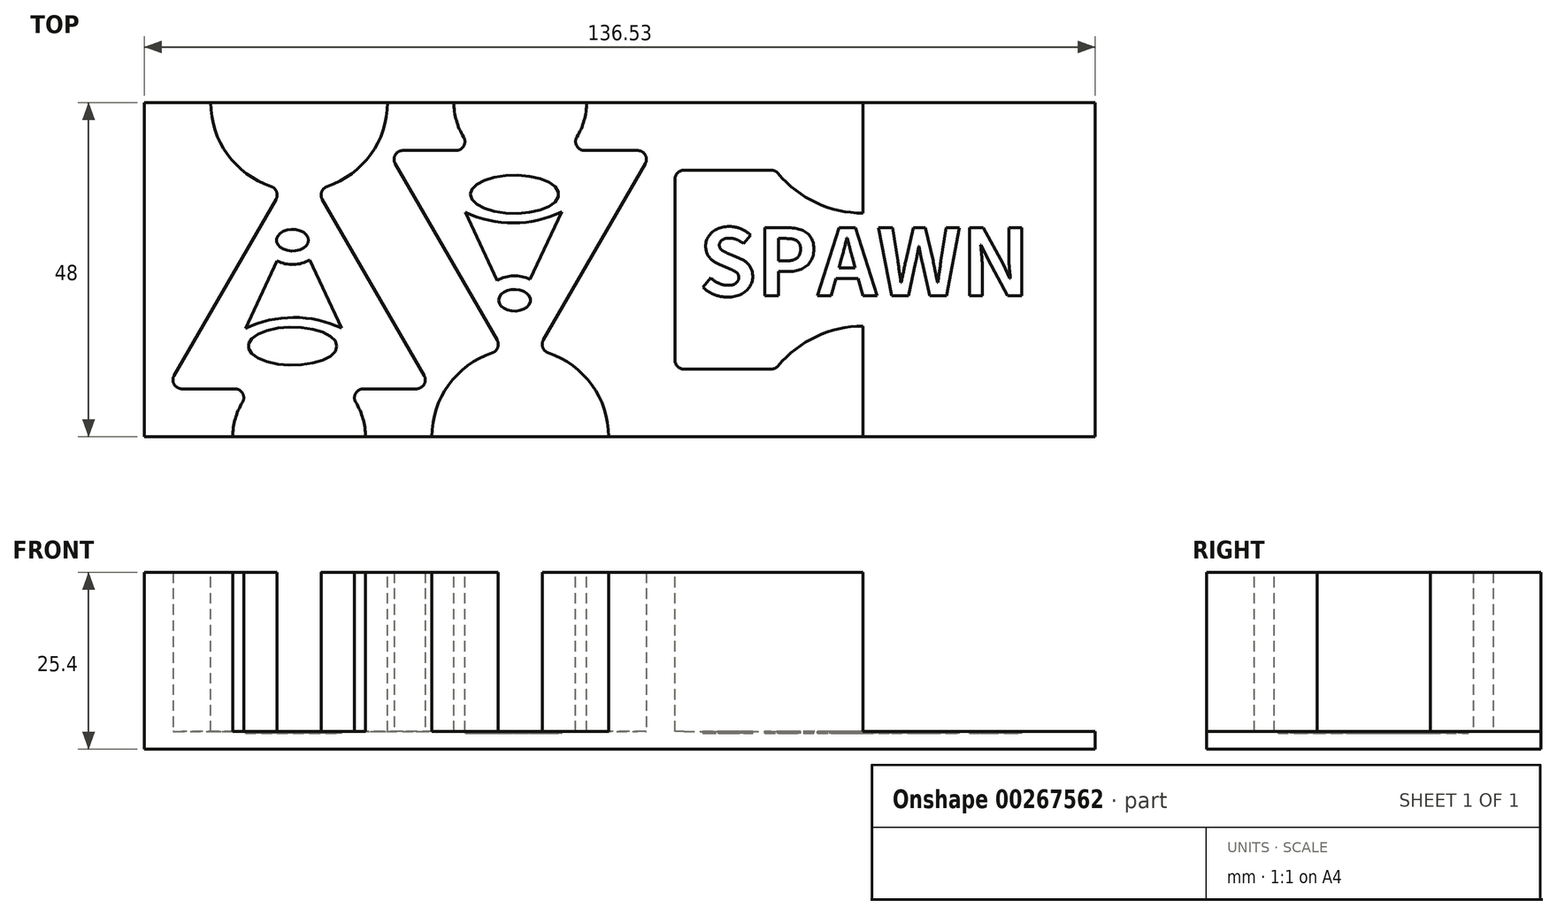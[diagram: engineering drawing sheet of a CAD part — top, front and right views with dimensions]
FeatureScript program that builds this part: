
annotation { "Feature Type Name" : "Feature", "Feature Type Description" : "" }
export const myFeature = defineFeature(function(context is Context, id is Id, definition is map)
    precondition{}
    {
        {
            var Q0;
            Q0=qCreatedBy(makeId("Top.planeOp"),FACE);
            var sketch = newSketch(context, id + "F0", { "sketchPlane" : qUnion([Q0])});
            skLineSegment(sketch, "E0.bottom", {"start": v(0, 0) * mm, "end": v(136.53, 0) * mm});
            skLineSegment(sketch, "E0.top", {"start": v(0, 48) * mm, "end": v(136.53, 48) * mm});
            skLineSegment(sketch, "E0.left", {"start": v(0, 0) * mm, "end": v(0, 48) * mm});
            skLineSegment(sketch, "E0.right", {"start": v(136.53, 0) * mm, "end": v(136.53, 48) * mm});
            skSolve(sketch);
        }
        {
            var Q0;
            Q0=makeQuery(id+"F0.imprint","IMPRINT",FACE,{"disambiguationData":[TD([[makeQuery(id+"F0.imprint","IMPRINT",EDGE,{"derivedFrom":sQuery(id+"F0.wireOp",EDGE,"E0.bottom")}),1.0]])]});
            extrude(context, id + "F1", {"entities" : qUnion([Q0]), "depth" : 25.4 * mm});
        }
        {
            var Q0;
            Q0=makeQuery(id+"F1.opExtrude","CAP_FACE",FACE,{"disambiguationData":[OSD([sQuery(id+"F0.wireOp",EDGE,"E0.bottom"),sQuery(id+"F0.wireOp",EDGE,"E0.top"),sQuery(id+"F0.wireOp",EDGE,"E0.left"),sQuery(id+"F0.wireOp",EDGE,"E0.right")])],"isStart":false});
            var sketch = newSketch(context, id + "F2", { "sketchPlane" : qUnion([Q0])});
            skCircle(sketch, "E1.cCircle", {"center": v(22.23, 17.88) * mm, "radius": 11 * mm, "construction": true});
            skLineSegment(sketch, "E1.0", {"start": v(22.23, 39.87) * mm, "end": v(41.28, 6.88) * mm});
            skLineSegment(sketch, "E1.1", {"start": v(41.28, 6.88) * mm, "end": v(3.18, 6.88) * mm});
            skLineSegment(sketch, "E1.2", {"start": v(3.17, 6.88) * mm, "end": v(22.23, 39.87) * mm});
            skPoint(sketch, "E1.0.midPoint", {"position": v(31.75, 23.38) * mm});
            skLineSegment(sketch, "E2", {"start": v(0, 24) * mm, "end": v(136.53, 24) * mm, "construction": true});
            skPoint(sketch, "E2.startSnap0", {"position": v(0, 24) * mm});
            skLineSegment(sketch, "E3", {"start": v(22.23, 48) * mm, "end": v(22.23, 0) * mm, "construction": true});
            skPoint(sketch, "E3.endSnap0", {"position": v(22.23, 6.88) * mm});
            skCircle(sketch, "E4", {"center": v(22.23, 48) * mm, "radius": 12.7 * mm});
            skCircle(sketch, "E5", {"center": v(22.22, 0) * mm, "radius": 9.53 * mm});
            skCircle(sketch, "E6.cCircle", {"center": v(53.97, 30.12) * mm, "radius": 11 * mm, "construction": true});
            skLineSegment(sketch, "E6.0", {"start": v(53.98, 8.12) * mm, "end": v(34.93, 41.12) * mm});
            skLineSegment(sketch, "E6.1", {"start": v(34.93, 41.12) * mm, "end": v(73.02, 41.12) * mm});
            skLineSegment(sketch, "E6.2", {"start": v(73.02, 41.12) * mm, "end": v(53.97, 8.13) * mm});
            skPoint(sketch, "E6.0.midPoint", {"position": v(44.45, 24.62) * mm});
            skLineSegment(sketch, "E7", {"start": v(136.53, 24) * mm, "end": v(0, 24) * mm, "construction": true});
            skPoint(sketch, "E7.startSnap0", {"position": v(122.49, -12.24) * mm});
            skLineSegment(sketch, "E8", {"start": v(53.98, 0) * mm, "end": v(53.98, 48) * mm, "construction": true});
            skPoint(sketch, "E8.endSnap0", {"position": v(53.98, 41.12) * mm});
            skCircle(sketch, "E9", {"center": v(53.98, 0) * mm, "radius": 12.7 * mm});
            skCircle(sketch, "E10", {"center": v(53.98, 48) * mm, "radius": 9.53 * mm});
            skLineSegment(sketch, "E11.bottom", {"start": v(76.2, 38.29) * mm, "end": v(130.17, 38.29) * mm});
            skLineSegment(sketch, "E11.top", {"start": v(76.2, 9.71) * mm, "end": v(130.17, 9.71) * mm});
            skLineSegment(sketch, "E11.left", {"start": v(76.2, 38.29) * mm, "end": v(76.2, 9.71) * mm});
            skLineSegment(sketch, "E11.right", {"start": v(130.18, 38.29) * mm, "end": v(130.18, 9.71) * mm});
            skCircle(sketch, "E12", {"center": v(103.19, 48) * mm, "radius": 15.88 * mm});
            skPoint(sketch, "E13.startSnap0", {"position": v(103.19, 9.71) * mm});
            skLineSegment(sketch, "E14", {"start": v(103.19, 0) * mm, "end": v(103.19, 48) * mm});
            skCircle(sketch, "E15", {"center": v(103.19, 0) * mm, "radius": 15.88 * mm});
            skSolve(sketch);
        }
        {
            var Q0;
            {var subQ1=sQuery(id+"F2.wireOp",EDGE,"E1.1");var subQ7=sQuery(id+"F2.wireOp",EDGE,"E1.0");var subQ8=makeQuery(id+"F2.imprint","INTERSECT",VERTEX,{"derivedFrom":[subQ7,subQ1]});Q0=makeQuery(id+"F2.imprint","IMPRINT",FACE,{"disambiguationData":[TD([[makeQuery(id+"F2.imprint","IMPRINT",EDGE,{"disambiguationData":[TD([[subQ8,1.0]])],"derivedFrom":subQ7}),-1.0]])]});}
            var Q1;
            {var subQ0=sQuery(id+"F2.wireOp",EDGE,"E5");var subQ1=sQuery(id+"F2.wireOp",EDGE,"E1.1");var subQ2=makeQuery(id+"F2.imprint","INTERSECT",VERTEX,{"disambiguationData":[OD(0.0)],"derivedFrom":[subQ1,subQ0]});Q1=makeQuery(id+"F2.imprint","IMPRINT",FACE,{"disambiguationData":[TD([[makeQuery(id+"F2.imprint","IMPRINT",EDGE,{"disambiguationData":[TD([[subQ2,-1.0]])],"derivedFrom":subQ1}),-1.0]])]});}
            var Q2;
            {var subQ0=sQuery(id+"F2.wireOp",EDGE,"E5");var subQ1=sQuery(id+"F2.wireOp",EDGE,"E1.1");var subQ2=makeQuery(id+"F2.imprint","INTERSECT",VERTEX,{"disambiguationData":[OD(0.0)],"derivedFrom":[subQ1,subQ0]});Q2=makeQuery(id+"F2.imprint","IMPRINT",FACE,{"disambiguationData":[TD([[makeQuery(id+"F2.imprint","IMPRINT",EDGE,{"disambiguationData":[TD([[subQ2,-1.0]])],"derivedFrom":subQ1}),1.0]])]});}
            var Q3;
            {var subQ1=sQuery(id+"F2.wireOp",EDGE,"E1.0");var subQ5=sQuery(id+"F2.wireOp",EDGE,"E1.2");var subQ8=makeQuery(id+"F2.imprint","INTERSECT",VERTEX,{"derivedFrom":[subQ1,subQ5]});Q3=makeQuery(id+"F2.imprint","IMPRINT",FACE,{"disambiguationData":[TD([[makeQuery(id+"F2.imprint","IMPRINT",EDGE,{"disambiguationData":[TD([[subQ8,-1.0]])],"derivedFrom":subQ1}),1.0]])]});}
            var Q4;
            {var subQ0=sQuery(id+"F2.wireOp",EDGE,"E1.2");var subQ1=sQuery(id+"F2.wireOp",EDGE,"E1.0");var subQ2=makeQuery(id+"F2.imprint","INTERSECT",VERTEX,{"derivedFrom":[subQ1,subQ0]});Q4=makeQuery(id+"F2.imprint","IMPRINT",FACE,{"disambiguationData":[TD([[makeQuery(id+"F2.imprint","IMPRINT",EDGE,{"disambiguationData":[TD([[subQ2,-1.0]])],"derivedFrom":subQ1}),-1.0]])]});}
            var Q5;
            {var subQ0=sQuery(id+"F2.wireOp",EDGE,"E10");var subQ1=sQuery(id+"F2.wireOp",EDGE,"E6.1");var subQ2=makeQuery(id+"F2.imprint","INTERSECT",VERTEX,{"disambiguationData":[OD(0.0)],"derivedFrom":[subQ1,subQ0]});Q5=makeQuery(id+"F2.imprint","IMPRINT",FACE,{"disambiguationData":[TD([[makeQuery(id+"F2.imprint","IMPRINT",EDGE,{"disambiguationData":[TD([[subQ2,-1.0]])],"derivedFrom":subQ1}),-1.0]])]});}
            var Q6;
            {var subQ0=sQuery(id+"F2.wireOp",EDGE,"E10");var subQ1=sQuery(id+"F2.wireOp",EDGE,"E6.1");var subQ2=makeQuery(id+"F2.imprint","INTERSECT",VERTEX,{"disambiguationData":[OD(0.0)],"derivedFrom":[subQ1,subQ0]});Q6=makeQuery(id+"F2.imprint","IMPRINT",FACE,{"disambiguationData":[TD([[makeQuery(id+"F2.imprint","IMPRINT",EDGE,{"disambiguationData":[TD([[subQ2,-1.0]])],"derivedFrom":subQ1}),1.0]])]});}
            var Q7;
            {var subQ1=sQuery(id+"F2.wireOp",EDGE,"E6.1");var subQ5=sQuery(id+"F2.wireOp",EDGE,"E6.0");var subQ6=makeQuery(id+"F2.imprint","INTERSECT",VERTEX,{"derivedFrom":[subQ5,subQ1]});Q7=makeQuery(id+"F2.imprint","IMPRINT",FACE,{"disambiguationData":[TD([[makeQuery(id+"F2.imprint","IMPRINT",EDGE,{"disambiguationData":[TD([[subQ6,1.0]])],"derivedFrom":subQ5}),-1.0]])]});}
            var Q8;
            {var subQ0=sQuery(id+"F2.wireOp",EDGE,"E6.2");var subQ1=sQuery(id+"F2.wireOp",EDGE,"E6.0");var subQ2=makeQuery(id+"F2.imprint","INTERSECT",VERTEX,{"derivedFrom":[subQ1,subQ0]});Q8=makeQuery(id+"F2.imprint","IMPRINT",FACE,{"disambiguationData":[TD([[makeQuery(id+"F2.imprint","IMPRINT",EDGE,{"disambiguationData":[TD([[subQ2,-1.0]])],"derivedFrom":subQ1}),-1.0]])]});}
            var Q9;
            {var subQ1=sQuery(id+"F2.wireOp",EDGE,"E6.2");var subQ6=sQuery(id+"F2.wireOp",EDGE,"E6.0");var subQ8=makeQuery(id+"F2.imprint","INTERSECT",VERTEX,{"derivedFrom":[subQ6,subQ1]});Q9=makeQuery(id+"F2.imprint","IMPRINT",FACE,{"disambiguationData":[TD([[makeQuery(id+"F2.imprint","IMPRINT",EDGE,{"disambiguationData":[TD([[subQ8,-1.0]])],"derivedFrom":subQ6}),1.0]])]});}
            var Q10;
            {var subQ5=sQuery(id+"F2.wireOp",EDGE,"E11.left");Q10=makeQuery(id+"F2.imprint","IMPRINT",FACE,{"disambiguationData":[TD([[makeQuery(id+"F2.imprint","IMPRINT",EDGE,{"derivedFrom":subQ5}),1.0]])]});}
            var Q11;
            {var subQ0=sQuery(id+"F2.wireOp",EDGE,"E12");var subQ1=sQuery(id+"F2.wireOp",EDGE,"E11.bottom");var subQ2=makeQuery(id+"F2.imprint","INTERSECT",VERTEX,{"disambiguationData":[OD(0.0)],"derivedFrom":[subQ1,subQ0]});Q11=makeQuery(id+"F2.imprint","IMPRINT",FACE,{"disambiguationData":[TD([[makeQuery(id+"F2.imprint","IMPRINT",EDGE,{"disambiguationData":[TD([[subQ2,-1.0]])],"derivedFrom":subQ1}),-1.0]])]});}
            var Q12;
            {var subQ0=sQuery(id+"F2.wireOp",EDGE,"E14");var subQ1=sQuery(id+"F2.wireOp",EDGE,"E11.bottom");var subQ2=makeQuery(id+"F2.imprint","INTERSECT",VERTEX,{"derivedFrom":[subQ1,subQ0]});Q12=makeQuery(id+"F2.imprint","IMPRINT",FACE,{"disambiguationData":[TD([[makeQuery(id+"F2.imprint","IMPRINT",EDGE,{"disambiguationData":[TD([[subQ2,-1.0]])],"derivedFrom":subQ1}),-1.0]])]});}
            var Q13;
            {var subQ0=sQuery(id+"F2.wireOp",EDGE,"E14");var subQ1=sQuery(id+"F2.wireOp",EDGE,"E11.bottom");var subQ2=makeQuery(id+"F2.imprint","INTERSECT",VERTEX,{"derivedFrom":[subQ1,subQ0]});Q13=makeQuery(id+"F2.imprint","IMPRINT",FACE,{"disambiguationData":[TD([[makeQuery(id+"F2.imprint","IMPRINT",EDGE,{"disambiguationData":[TD([[subQ2,-1.0]])],"derivedFrom":subQ1}),1.0]])]});}
            var Q14;
            {var subQ0=sQuery(id+"F2.wireOp",EDGE,"E12");var subQ1=sQuery(id+"F2.wireOp",EDGE,"E11.bottom");var subQ2=makeQuery(id+"F2.imprint","INTERSECT",VERTEX,{"disambiguationData":[OD(0.0)],"derivedFrom":[subQ1,subQ0]});Q14=makeQuery(id+"F2.imprint","IMPRINT",FACE,{"disambiguationData":[TD([[makeQuery(id+"F2.imprint","IMPRINT",EDGE,{"disambiguationData":[TD([[subQ2,-1.0]])],"derivedFrom":subQ1}),1.0]])]});}
            var Q15;
            {var subQ0=sQuery(id+"F2.wireOp",EDGE,"E11.right");Q15=makeQuery(id+"F2.imprint","IMPRINT",FACE,{"disambiguationData":[TD([[makeQuery(id+"F2.imprint","IMPRINT",EDGE,{"derivedFrom":subQ0}),-1.0]])]});}
            var Q16;
            {var subQ0=sQuery(id+"F2.wireOp",EDGE,"E14");var subQ1=sQuery(id+"F2.wireOp",EDGE,"E11.top");var subQ2=makeQuery(id+"F2.imprint","INTERSECT",VERTEX,{"derivedFrom":[subQ1,subQ0]});Q16=makeQuery(id+"F2.imprint","IMPRINT",FACE,{"disambiguationData":[TD([[makeQuery(id+"F2.imprint","IMPRINT",EDGE,{"disambiguationData":[TD([[subQ2,-1.0]])],"derivedFrom":subQ1}),1.0]])]});}
            var Q17;
            {var subQ0=sQuery(id+"F2.wireOp",EDGE,"E15");var subQ1=sQuery(id+"F2.wireOp",EDGE,"E11.top");var subQ2=makeQuery(id+"F2.imprint","INTERSECT",VERTEX,{"disambiguationData":[OD(0.0)],"derivedFrom":[subQ1,subQ0]});Q17=makeQuery(id+"F2.imprint","IMPRINT",FACE,{"disambiguationData":[TD([[makeQuery(id+"F2.imprint","IMPRINT",EDGE,{"disambiguationData":[TD([[subQ2,-1.0]])],"derivedFrom":subQ1}),1.0]])]});}
            var Q18;
            {var subQ0=sQuery(id+"F2.wireOp",EDGE,"E15");var subQ1=sQuery(id+"F2.wireOp",EDGE,"E11.top");var subQ2=makeQuery(id+"F2.imprint","INTERSECT",VERTEX,{"disambiguationData":[OD(0.0)],"derivedFrom":[subQ1,subQ0]});Q18=makeQuery(id+"F2.imprint","IMPRINT",FACE,{"disambiguationData":[TD([[makeQuery(id+"F2.imprint","IMPRINT",EDGE,{"disambiguationData":[TD([[subQ2,-1.0]])],"derivedFrom":subQ1}),-1.0]])]});}
            var Q19;
            {var subQ0=sQuery(id+"F2.wireOp",EDGE,"E14");var subQ1=sQuery(id+"F2.wireOp",EDGE,"E11.top");var subQ2=makeQuery(id+"F2.imprint","INTERSECT",VERTEX,{"derivedFrom":[subQ1,subQ0]});Q19=makeQuery(id+"F2.imprint","IMPRINT",FACE,{"disambiguationData":[TD([[makeQuery(id+"F2.imprint","IMPRINT",EDGE,{"disambiguationData":[TD([[subQ2,-1.0]])],"derivedFrom":subQ1}),-1.0]])]});}
            extrude(context, id + "F3", {"entities" : qUnion([Q0, Q1, Q2, Q3, Q4, Q5, Q6, Q7, Q8, Q9, Q10, Q11, Q12, Q13, Q14, Q15, Q16, Q17, Q18, Q19]), "operationType" : NewBodyOperationType.REMOVE, "oppositeDirection" : true, "depth" : 22.86 * mm});
        }
        {
            var Q0;
            Q0=makeQuery(id+"F3.boolean.opBoolean","COPY",FACE,{"derivedFrom":makeQuery(id+"F3.opExtrude","CAP_FACE",FACE,{"disambiguationData":[OSD([sQuery(id+"F0.wireOp",EDGE,"E0.bottom"),sQuery(id+"F0.wireOp",EDGE,"E0.top"),sQuery(id+"F2.wireOp",EDGE,"E11.bottom"),sQuery(id+"F2.wireOp",EDGE,"E11.top"),sQuery(id+"F2.wireOp",EDGE,"E11.left"),sQuery(id+"F2.wireOp",EDGE,"E11.right"),sQuery(id+"F2.wireOp",EDGE,"E12"),sQuery(id+"F2.wireOp",EDGE,"E15")])],"isStart":false})});
            var sketch = newSketch(context, id + "F4", { "sketchPlane" : qUnion([Q0])});
            skText(sketch, "E16", { "text": "SPAWN", "fontName": "NotoSansCJKsc-Bold.otf"});
            skLineSegment(sketch, "E17", {"start": v(103.19, 50.68) * mm, "end": v(103.19, -4.65) * mm, "construction": true});
            skPoint(sketch, "E17.startSnap0", {"position": v(103.19, 48) * mm});
            skPoint(sketch, "E17.endSnap0", {"position": v(103.19, 0) * mm});
            skLineSegment(sketch, "E18", {"start": v(76.2, 24) * mm, "end": v(130.18, 24) * mm, "construction": true});
            skPoint(sketch, "E18.startSnap0", {"position": v(79.63, 24) * mm});
            skPoint(sketch, "E18.endSnap0", {"position": v(126.74, 24) * mm});
            skLineSegment(sketch, "E19", {"start": v(14.53, 15.54) * mm, "end": v(19.06, 25.26) * mm});
            skLineSegment(sketch, "E20", {"start": v(23.76, 25.4) * mm, "end": v(28.34, 15.59) * mm});
            skArc(sketch, "E21", {"start": v(28.34, 15.59) * mm, "mid": v(21.43, 17.13) * mm, "end": v(14.53, 15.54) * mm});
            skEllipse(sketch, "E22", {"center": v(21.27, 28.23) * mm, "majorRadius": 2.29 * mm, "minorRadius": 1.56 * mm, "majorAxis": v(1, 0)});
            skArc(sketch, "E23", {"start": v(19.06, 25.26) * mm, "mid": v(21.43, 24.74) * mm, "end": v(23.76, 25.4) * mm});
            skEllipse(sketch, "E24", {"center": v(21.27, 13.01) * mm, "majorRadius": 6.36 * mm, "minorRadius": 2.75 * mm, "majorAxis": v(1, 0)});
            skLineSegment(sketch, "E25", {"start": v(59.9, 32.3) * mm, "end": v(55.38, 22.58) * mm});
            skLineSegment(sketch, "E26", {"start": v(50.68, 22.44) * mm, "end": v(46.1, 32.26) * mm});
            skArc(sketch, "E27", {"start": v(46.1, 32.26) * mm, "mid": v(53, 30.71) * mm, "end": v(59.9, 32.3) * mm});
            skEllipse(sketch, "E28", {"center": v(53.16, 19.6) * mm, "majorRadius": 2.29 * mm, "minorRadius": 1.56 * mm, "majorAxis": v(-1, 0)});
            skArc(sketch, "E29", {"start": v(55.38, 22.58) * mm, "mid": v(53, 23.1) * mm, "end": v(50.68, 22.44) * mm});
            skEllipse(sketch, "E30", {"center": v(53.16, 34.83) * mm, "majorRadius": 6.36 * mm, "minorRadius": 2.75 * mm, "majorAxis": v(-1, 0)});
            skLineSegment(sketch, "E31", {"start": v(20.96, 51.27) * mm, "end": v(21.77, -7.94) * mm, "construction": true});
            skLineSegment(sketch, "E32", {"start": v(54.07, -7.72) * mm, "end": v(52.7, 58.9) * mm, "construction": true});
            const initialGuessF4  = {"E16": [0.07963, 0.02024, 1, 0, 0.00952]};
            skSetInitialGuess(sketch, initialGuessF4);
            skSolve(sketch);
        }
        {
            var Q0;
            Q0=makeQuery(id+"F4.imprint","IMPRINT",FACE,{"disambiguationData":[TD([[makeQuery(id+"F4.imprint","IMPRINT",EDGE,{"derivedFrom":sQuery(id+"F4.wireOp",EDGE,"E16.sketch_text.stroke-0")}),1.0]])]});
            var Q1;
            Q1=makeQuery(id+"F4.imprint","IMPRINT",FACE,{"disambiguationData":[TD([[makeQuery(id+"F4.imprint","IMPRINT",EDGE,{"derivedFrom":sQuery(id+"F4.wireOp",EDGE,"E16.sketch_text.stroke-16")}),1.0]])]});
            var Q2;
            Q2=makeQuery(id+"F4.imprint","IMPRINT",FACE,{"disambiguationData":[TD([[makeQuery(id+"F4.imprint","IMPRINT",EDGE,{"derivedFrom":sQuery(id+"F4.wireOp",EDGE,"E16.sketch_text.stroke-28")}),1.0]])]});
            var Q3;
            Q3=makeQuery(id+"F4.imprint","IMPRINT",FACE,{"disambiguationData":[TD([[makeQuery(id+"F4.imprint","IMPRINT",EDGE,{"derivedFrom":sQuery(id+"F4.wireOp",EDGE,"E16.sketch_text.stroke-42")}),1.0]])]});
            var Q4;
            Q4=makeQuery(id+"F4.imprint","IMPRINT",FACE,{"disambiguationData":[TD([[makeQuery(id+"F4.imprint","IMPRINT",EDGE,{"derivedFrom":sQuery(id+"F4.wireOp",EDGE,"E16.sketch_text.stroke-64")}),1.0]])]});
            var Q5;
            Q5=makeQuery(id+"F4.imprint","IMPRINT",FACE,{"disambiguationData":[TD([[makeQuery(id+"F4.imprint","IMPRINT",EDGE,{"derivedFrom":sQuery(id+"F4.wireOp",EDGE,"E30")}),1.0]])]});
            var Q6;
            Q6=makeQuery(id+"F4.imprint","IMPRINT",FACE,{"disambiguationData":[TD([[makeQuery(id+"F4.imprint","IMPRINT",EDGE,{"derivedFrom":sQuery(id+"F4.wireOp",EDGE,"E25")}),-1.0]])]});
            var Q7;
            Q7=makeQuery(id+"F4.imprint","IMPRINT",FACE,{"disambiguationData":[TD([[makeQuery(id+"F4.imprint","IMPRINT",EDGE,{"derivedFrom":sQuery(id+"F4.wireOp",EDGE,"E28")}),1.0]])]});
            var Q8;
            Q8=makeQuery(id+"F4.imprint","IMPRINT",FACE,{"disambiguationData":[TD([[makeQuery(id+"F4.imprint","IMPRINT",EDGE,{"derivedFrom":sQuery(id+"F4.wireOp",EDGE,"E24")}),1.0]])]});
            var Q9;
            Q9=makeQuery(id+"F4.imprint","IMPRINT",FACE,{"disambiguationData":[TD([[makeQuery(id+"F4.imprint","IMPRINT",EDGE,{"derivedFrom":sQuery(id+"F4.wireOp",EDGE,"E19")}),-1.0]])]});
            var Q10;
            Q10=makeQuery(id+"F4.imprint","IMPRINT",FACE,{"disambiguationData":[TD([[makeQuery(id+"F4.imprint","IMPRINT",EDGE,{"derivedFrom":sQuery(id+"F4.wireOp",EDGE,"E22")}),1.0]])]});
            extrude(context, id + "F5", {"entities" : qUnion([Q0, Q1, Q2, Q3, Q4, Q5, Q6, Q7, Q8, Q9, Q10]), "operationType" : NewBodyOperationType.REMOVE, "oppositeDirection" : true, "depth" : 0.25 * mm});
        }
        {
            var Q0;
            {var subQ0=sQuery(id+"F2.wireOp",EDGE,"E5");var subQ1=sQuery(id+"F2.wireOp",EDGE,"E1.1");Q0=makeQuery(id+"F3.boolean.opBoolean","COPY",EDGE,{"derivedFrom":makeQuery(id+"F3.opExtrude","SWEPT_EDGE",EDGE,{"disambiguationData":[OSD([subQ1,subQ0]),TDD([makeQuery(id+"F2.imprint","INTERSECT",VERTEX,{"disambiguationData":[OD(1.0)],"derivedFrom":[subQ1,subQ0]})])]})});}
            var Q1;
            {var subQ0=sQuery(id+"F2.wireOp",EDGE,"E5");var subQ1=sQuery(id+"F2.wireOp",EDGE,"E1.1");Q1=makeQuery(id+"F3.boolean.opBoolean","COPY",EDGE,{"derivedFrom":makeQuery(id+"F3.opExtrude","SWEPT_EDGE",EDGE,{"disambiguationData":[OSD([subQ1,subQ0]),TDD([makeQuery(id+"F2.imprint","INTERSECT",VERTEX,{"disambiguationData":[OD(0.0)],"derivedFrom":[subQ1,subQ0]})])]})});}
            var Q2;
            Q2=makeQuery(id+"F3.boolean.opBoolean","COPY",EDGE,{"derivedFrom":makeQuery(id+"F3.opExtrude","SWEPT_EDGE",EDGE,{"disambiguationData":[OSD([sQuery(id+"F2.wireOp",EDGE,"E1.2"),sQuery(id+"F2.wireOp",EDGE,"E4")])]})});
            var Q3;
            Q3=makeQuery(id+"F3.boolean.opBoolean","COPY",EDGE,{"derivedFrom":makeQuery(id+"F3.opExtrude","SWEPT_EDGE",EDGE,{"disambiguationData":[OSD([sQuery(id+"F2.wireOp",EDGE,"E1.0"),sQuery(id+"F2.wireOp",EDGE,"E4")])]})});
            var Q4;
            {var subQ0=sQuery(id+"F2.wireOp",EDGE,"E4");var subQ1=sQuery(id+"F0.wireOp",EDGE,"E0.top");Q4=makeQuery(id+"F3.boolean.opBoolean","COPY",EDGE,{"derivedFrom":makeQuery(id+"F3.opExtrude","SWEPT_EDGE",EDGE,{"disambiguationData":[OSD([subQ1,subQ0]),TDD([makeQuery(id+"F2.imprint","INTERSECT",VERTEX,{"disambiguationData":[OD(0.0)],"derivedFrom":[makeQuery(id+"F1.opExtrude","CAP_EDGE",EDGE,{"disambiguationData":[OSD([subQ1])],"isStart":false}),subQ0]})])]})});}
            var Q5;
            {var subQ0=sQuery(id+"F2.wireOp",EDGE,"E4");var subQ1=sQuery(id+"F0.wireOp",EDGE,"E0.top");Q5=makeQuery(id+"F3.boolean.opBoolean","COPY",EDGE,{"derivedFrom":makeQuery(id+"F3.opExtrude","SWEPT_EDGE",EDGE,{"disambiguationData":[OSD([subQ1,subQ0]),TDD([makeQuery(id+"F2.imprint","INTERSECT",VERTEX,{"disambiguationData":[OD(1.0)],"derivedFrom":[makeQuery(id+"F1.opExtrude","CAP_EDGE",EDGE,{"disambiguationData":[OSD([subQ1])],"isStart":false}),subQ0]})])]})});}
            var Q6;
            {var subQ0=sQuery(id+"F2.wireOp",EDGE,"E10");var subQ1=sQuery(id+"F0.wireOp",EDGE,"E0.top");Q6=makeQuery(id+"F3.boolean.opBoolean","COPY",EDGE,{"derivedFrom":makeQuery(id+"F3.opExtrude","SWEPT_EDGE",EDGE,{"disambiguationData":[OSD([subQ1,subQ0]),TDD([makeQuery(id+"F2.imprint","INTERSECT",VERTEX,{"disambiguationData":[OD(0.0)],"derivedFrom":[makeQuery(id+"F1.opExtrude","CAP_EDGE",EDGE,{"disambiguationData":[OSD([subQ1])],"isStart":false}),subQ0]})])]})});}
            var Q7;
            {var subQ0=sQuery(id+"F2.wireOp",EDGE,"E10");var subQ1=sQuery(id+"F2.wireOp",EDGE,"E6.1");Q7=makeQuery(id+"F3.boolean.opBoolean","COPY",EDGE,{"derivedFrom":makeQuery(id+"F3.opExtrude","SWEPT_EDGE",EDGE,{"disambiguationData":[OSD([subQ1,subQ0]),TDD([makeQuery(id+"F2.imprint","INTERSECT",VERTEX,{"disambiguationData":[OD(0.0)],"derivedFrom":[subQ1,subQ0]})])]})});}
            var Q8;
            Q8=makeQuery(id+"F3.boolean.opBoolean","COPY",EDGE,{"derivedFrom":makeQuery(id+"F3.opExtrude","SWEPT_EDGE",EDGE,{"disambiguationData":[OSD([sQuery(id+"F2.wireOp",EDGE,"E6.0"),sQuery(id+"F2.wireOp",EDGE,"E6.1")])]})});
            var Q9;
            Q9=makeQuery(id+"F3.boolean.opBoolean","COPY",EDGE,{"derivedFrom":makeQuery(id+"F3.opExtrude","SWEPT_EDGE",EDGE,{"disambiguationData":[OSD([sQuery(id+"F2.wireOp",EDGE,"E6.0"),sQuery(id+"F2.wireOp",EDGE,"E9")])]})});
            var Q10;
            Q10=makeQuery(id+"F3.boolean.opBoolean","COPY",EDGE,{"derivedFrom":makeQuery(id+"F3.opExtrude","SWEPT_EDGE",EDGE,{"disambiguationData":[OSD([sQuery(id+"F2.wireOp",EDGE,"E1.0"),sQuery(id+"F2.wireOp",EDGE,"E1.1")])]})});
            var Q11;
            Q11=makeQuery(id+"F3.boolean.opBoolean","COPY",EDGE,{"derivedFrom":makeQuery(id+"F3.opExtrude","SWEPT_EDGE",EDGE,{"disambiguationData":[OSD([sQuery(id+"F2.wireOp",EDGE,"E6.1"),sQuery(id+"F2.wireOp",EDGE,"E6.2")])]})});
            var Q12;
            {var subQ0=sQuery(id+"F2.wireOp",EDGE,"E10");var subQ1=sQuery(id+"F2.wireOp",EDGE,"E6.1");Q12=makeQuery(id+"F3.boolean.opBoolean","COPY",EDGE,{"derivedFrom":makeQuery(id+"F3.opExtrude","SWEPT_EDGE",EDGE,{"disambiguationData":[OSD([subQ1,subQ0]),TDD([makeQuery(id+"F2.imprint","INTERSECT",VERTEX,{"disambiguationData":[OD(1.0)],"derivedFrom":[subQ1,subQ0]})])]})});}
            var Q13;
            {var subQ0=sQuery(id+"F2.wireOp",EDGE,"E10");var subQ1=sQuery(id+"F0.wireOp",EDGE,"E0.top");Q13=makeQuery(id+"F3.boolean.opBoolean","COPY",EDGE,{"derivedFrom":makeQuery(id+"F3.opExtrude","SWEPT_EDGE",EDGE,{"disambiguationData":[OSD([subQ1,subQ0]),TDD([makeQuery(id+"F2.imprint","INTERSECT",VERTEX,{"disambiguationData":[OD(1.0)],"derivedFrom":[makeQuery(id+"F1.opExtrude","CAP_EDGE",EDGE,{"disambiguationData":[OSD([subQ1])],"isStart":false}),subQ0]})])]})});}
            var Q14;
            Q14=makeQuery(id+"F3.boolean.opBoolean","COPY",EDGE,{"derivedFrom":makeQuery(id+"F3.opExtrude","SWEPT_EDGE",EDGE,{"disambiguationData":[OSD([sQuery(id+"F2.wireOp",EDGE,"E6.2"),sQuery(id+"F2.wireOp",EDGE,"E9")])]})});
            var Q15;
            {var subQ0=sQuery(id+"F2.wireOp",EDGE,"E9");var subQ1=sQuery(id+"F0.wireOp",EDGE,"E0.bottom");Q15=makeQuery(id+"F3.boolean.opBoolean","COPY",EDGE,{"derivedFrom":makeQuery(id+"F3.opExtrude","SWEPT_EDGE",EDGE,{"disambiguationData":[OSD([subQ1,subQ0]),TDD([makeQuery(id+"F2.imprint","INTERSECT",VERTEX,{"disambiguationData":[OD(0.0)],"derivedFrom":[makeQuery(id+"F1.opExtrude","CAP_EDGE",EDGE,{"disambiguationData":[OSD([subQ1])],"isStart":false}),subQ0]})])]})});}
            var Q16;
            {var subQ0=sQuery(id+"F2.wireOp",EDGE,"E5");var subQ1=sQuery(id+"F0.wireOp",EDGE,"E0.bottom");Q16=makeQuery(id+"F3.boolean.opBoolean","COPY",EDGE,{"derivedFrom":makeQuery(id+"F3.opExtrude","SWEPT_EDGE",EDGE,{"disambiguationData":[OSD([subQ1,subQ0]),TDD([makeQuery(id+"F2.imprint","INTERSECT",VERTEX,{"disambiguationData":[OD(1.0)],"derivedFrom":[makeQuery(id+"F1.opExtrude","CAP_EDGE",EDGE,{"disambiguationData":[OSD([subQ1])],"isStart":false}),subQ0]})])]})});}
            var Q17;
            {var subQ0=sQuery(id+"F2.wireOp",EDGE,"E5");var subQ1=sQuery(id+"F0.wireOp",EDGE,"E0.bottom");Q17=makeQuery(id+"F3.boolean.opBoolean","COPY",EDGE,{"derivedFrom":makeQuery(id+"F3.opExtrude","SWEPT_EDGE",EDGE,{"disambiguationData":[OSD([subQ1,subQ0]),TDD([makeQuery(id+"F2.imprint","INTERSECT",VERTEX,{"disambiguationData":[OD(0.0)],"derivedFrom":[makeQuery(id+"F1.opExtrude","CAP_EDGE",EDGE,{"disambiguationData":[OSD([subQ1])],"isStart":false}),subQ0]})])]})});}
            var Q18;
            {var subQ0=sQuery(id+"F2.wireOp",EDGE,"E9");var subQ1=sQuery(id+"F0.wireOp",EDGE,"E0.bottom");Q18=makeQuery(id+"F3.boolean.opBoolean","COPY",EDGE,{"derivedFrom":makeQuery(id+"F3.opExtrude","SWEPT_EDGE",EDGE,{"disambiguationData":[OSD([subQ1,subQ0]),TDD([makeQuery(id+"F2.imprint","INTERSECT",VERTEX,{"disambiguationData":[OD(1.0)],"derivedFrom":[makeQuery(id+"F1.opExtrude","CAP_EDGE",EDGE,{"disambiguationData":[OSD([subQ1])],"isStart":false}),subQ0]})])]})});}
            var Q19;
            Q19=makeQuery(id+"F3.boolean.opBoolean","COPY",EDGE,{"derivedFrom":makeQuery(id+"F3.opExtrude","SWEPT_EDGE",EDGE,{"disambiguationData":[OSD([sQuery(id+"F2.wireOp",EDGE,"E11.bottom"),sQuery(id+"F2.wireOp",EDGE,"E11.left")])]})});
            var Q20;
            {var subQ0=sQuery(id+"F2.wireOp",EDGE,"E12");var subQ1=sQuery(id+"F2.wireOp",EDGE,"E11.bottom");Q20=makeQuery(id+"F3.boolean.opBoolean","COPY",EDGE,{"derivedFrom":makeQuery(id+"F3.opExtrude","SWEPT_EDGE",EDGE,{"disambiguationData":[OSD([subQ1,subQ0]),TDD([makeQuery(id+"F2.imprint","INTERSECT",VERTEX,{"disambiguationData":[OD(0.0)],"derivedFrom":[subQ1,subQ0]})])]})});}
            var Q21;
            {var subQ0=sQuery(id+"F2.wireOp",EDGE,"E12");var subQ1=sQuery(id+"F0.wireOp",EDGE,"E0.top");Q21=makeQuery(id+"F3.boolean.opBoolean","COPY",EDGE,{"derivedFrom":makeQuery(id+"F3.opExtrude","SWEPT_EDGE",EDGE,{"disambiguationData":[OSD([subQ1,subQ0]),TDD([makeQuery(id+"F2.imprint","INTERSECT",VERTEX,{"disambiguationData":[OD(0.0)],"derivedFrom":[makeQuery(id+"F1.opExtrude","CAP_EDGE",EDGE,{"disambiguationData":[OSD([subQ1])],"isStart":false}),subQ0]})])]})});}
            var Q22;
            Q22=makeQuery(id+"F3.boolean.opBoolean","COPY",EDGE,{"derivedFrom":makeQuery(id+"F3.opExtrude","SWEPT_EDGE",EDGE,{"disambiguationData":[OSD([sQuery(id+"F2.wireOp",EDGE,"E11.top"),sQuery(id+"F2.wireOp",EDGE,"E11.left")])]})});
            var Q23;
            {var subQ0=sQuery(id+"F2.wireOp",EDGE,"E15");var subQ1=sQuery(id+"F2.wireOp",EDGE,"E11.top");Q23=makeQuery(id+"F3.boolean.opBoolean","COPY",EDGE,{"derivedFrom":makeQuery(id+"F3.opExtrude","SWEPT_EDGE",EDGE,{"disambiguationData":[OSD([subQ1,subQ0]),TDD([makeQuery(id+"F2.imprint","INTERSECT",VERTEX,{"disambiguationData":[OD(0.0)],"derivedFrom":[subQ1,subQ0]})])]})});}
            var Q24;
            {var subQ0=sQuery(id+"F2.wireOp",EDGE,"E12");var subQ1=sQuery(id+"F2.wireOp",EDGE,"E11.bottom");Q24=makeQuery(id+"F3.boolean.opBoolean","COPY",EDGE,{"derivedFrom":makeQuery(id+"F3.opExtrude","SWEPT_EDGE",EDGE,{"disambiguationData":[OSD([subQ1,subQ0]),TDD([makeQuery(id+"F2.imprint","INTERSECT",VERTEX,{"disambiguationData":[OD(1.0)],"derivedFrom":[subQ1,subQ0]})])]})});}
            var Q25;
            {var subQ0=sQuery(id+"F2.wireOp",EDGE,"E12");var subQ1=sQuery(id+"F0.wireOp",EDGE,"E0.top");Q25=makeQuery(id+"F3.boolean.opBoolean","COPY",EDGE,{"derivedFrom":makeQuery(id+"F3.opExtrude","SWEPT_EDGE",EDGE,{"disambiguationData":[OSD([subQ1,subQ0]),TDD([makeQuery(id+"F2.imprint","INTERSECT",VERTEX,{"disambiguationData":[OD(1.0)],"derivedFrom":[makeQuery(id+"F1.opExtrude","CAP_EDGE",EDGE,{"disambiguationData":[OSD([subQ1])],"isStart":false}),subQ0]})])]})});}
            var Q26;
            Q26=makeQuery(id+"F3.boolean.opBoolean","COPY",EDGE,{"derivedFrom":makeQuery(id+"F3.opExtrude","SWEPT_EDGE",EDGE,{"disambiguationData":[OSD([sQuery(id+"F2.wireOp",EDGE,"E11.bottom"),sQuery(id+"F2.wireOp",EDGE,"E11.right")])]})});
            var Q27;
            Q27=makeQuery(id+"F3.boolean.opBoolean","COPY",EDGE,{"derivedFrom":makeQuery(id+"F3.opExtrude","SWEPT_EDGE",EDGE,{"disambiguationData":[OSD([sQuery(id+"F2.wireOp",EDGE,"E11.top"),sQuery(id+"F2.wireOp",EDGE,"E11.right")])]})});
            var Q28;
            {var subQ0=sQuery(id+"F2.wireOp",EDGE,"E15");var subQ1=sQuery(id+"F2.wireOp",EDGE,"E11.top");Q28=makeQuery(id+"F3.boolean.opBoolean","COPY",EDGE,{"derivedFrom":makeQuery(id+"F3.opExtrude","SWEPT_EDGE",EDGE,{"disambiguationData":[OSD([subQ1,subQ0]),TDD([makeQuery(id+"F2.imprint","INTERSECT",VERTEX,{"disambiguationData":[OD(1.0)],"derivedFrom":[subQ1,subQ0]})])]})});}
            var Q29;
            {var subQ0=sQuery(id+"F2.wireOp",EDGE,"E15");var subQ1=sQuery(id+"F0.wireOp",EDGE,"E0.bottom");Q29=makeQuery(id+"F3.boolean.opBoolean","COPY",EDGE,{"derivedFrom":makeQuery(id+"F3.opExtrude","SWEPT_EDGE",EDGE,{"disambiguationData":[OSD([subQ1,subQ0]),TDD([makeQuery(id+"F2.imprint","INTERSECT",VERTEX,{"disambiguationData":[OD(0.0)],"derivedFrom":[makeQuery(id+"F1.opExtrude","CAP_EDGE",EDGE,{"disambiguationData":[OSD([subQ1])],"isStart":false}),subQ0]})])]})});}
            var Q30;
            Q30=makeQuery(id+"F3.boolean.opBoolean","COPY",EDGE,{"derivedFrom":makeQuery(id+"F3.opExtrude","SWEPT_EDGE",EDGE,{"disambiguationData":[OSD([sQuery(id+"F2.wireOp",EDGE,"E1.1"),sQuery(id+"F2.wireOp",EDGE,"E1.2")])]})});
            fillet(context, id + "F6", {"entities" : qUnion([Q0, Q1, Q2, Q3, Q4, Q5, Q6, Q7, Q8, Q9, Q10, Q11, Q12, Q13, Q14, Q15, Q16, Q17, Q18, Q19, Q20, Q21, Q22, Q23, Q24, Q25, Q26, Q27, Q28, Q29, Q30]), "radius" : 1.27 * mm, "tangentPropagation" : true, "allowEdgeOverflow" : false});
        }
    });
